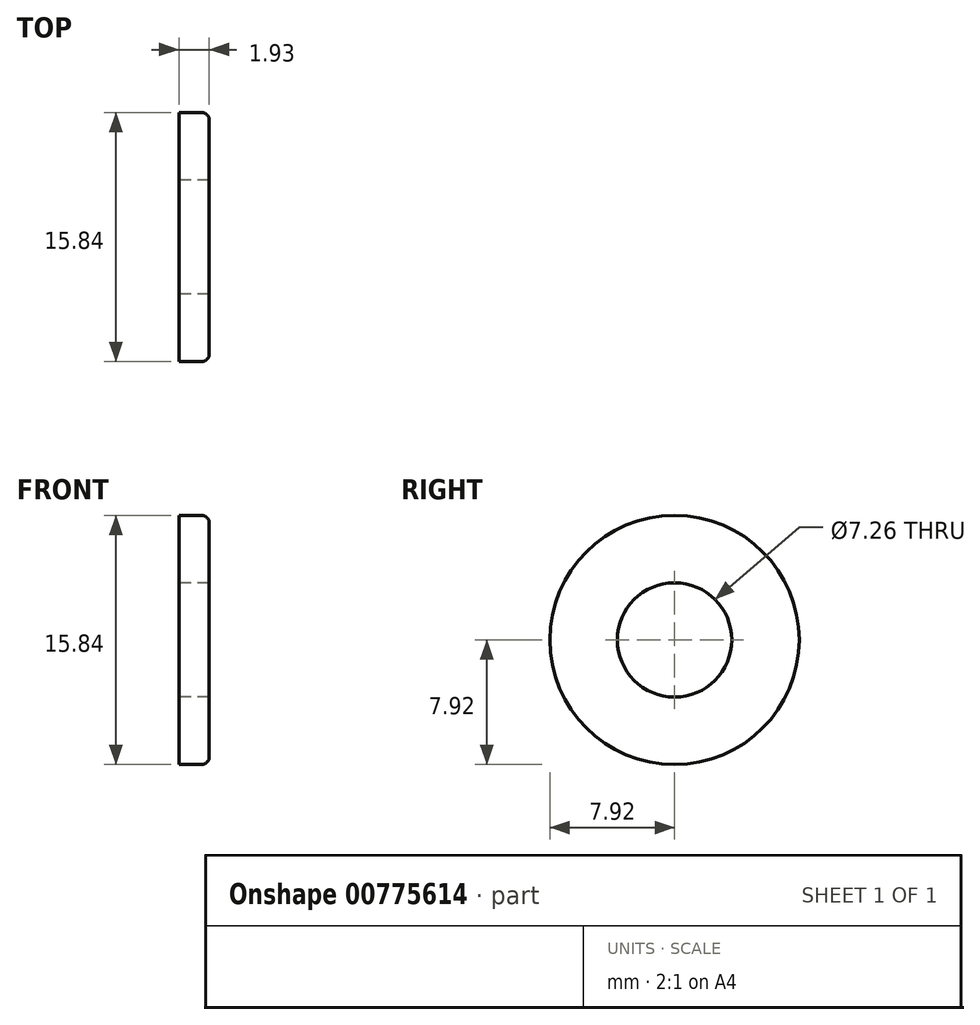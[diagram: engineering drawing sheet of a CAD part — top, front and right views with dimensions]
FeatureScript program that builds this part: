
annotation { "Feature Type Name" : "Feature", "Feature Type Description" : "" }
export const myFeature = defineFeature(function(context is Context, id is Id, definition is map)
    precondition{}
    {
        {
            var Q0;
            Q0=qCreatedBy(makeId("Right.planeOp"),FACE);
            var sketch = newSketch(context, id + "F0", { "sketchPlane" : qUnion([Q0])});
            skCircle(sketch, "E0", {"center": v(0, 0) * mm, "radius": 7.92 * mm});
            skCircle(sketch, "E1", {"center": v(0, 0) * mm, "radius": 3.63 * mm});
            skSolve(sketch);
        }
        {
            var Q0;
            Q0 = qSketchRegion(id + "F0", true);
            extrude(context, id + "F1", {"entities" : qUnion([Q0]), "depth" : 1.93 * mm, "offsetDistance" : 25.4 * mm});
        }
        {
            var Q0;
            Q0=makeQuery(id+"F1.opExtrude","CAP_EDGE",EDGE,{"disambiguationData":[OSD([sQuery(id+"F0.wireOp",EDGE,"E0")])],"isStart":false});
            fillet(context, id + "F2", {"entities" : qUnion([Q0]), "radius" : 0.5 * mm, "tangentPropagation" : true, "allowEdgeOverflow" : false});
        }
    });
